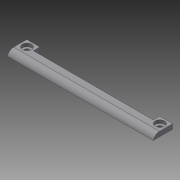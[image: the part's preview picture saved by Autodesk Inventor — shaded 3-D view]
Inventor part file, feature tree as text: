
AUTODESK INVENTOR PART (.ipt)
format: ipt  version: 2015 (Build 190159000, 159)  size: 122,368 bytes
history: native  units: mm
features: extrude x5, sketch x5, other x1, fillet x1
ambient origin geometry x8: Origin, YZ Plane, XZ Plane, XY Plane, X Axis, Y Axis, Z Axis, Center Point
bodies: Body1 (feature_tree), Body2 (feature_tree)
feature tree (12):
  other  "ソリッド1"
  extrude  "押し出し1"  Depth=90.0mm
  extrude  "押し出し2"  Depth=7.0mm
  extrude  "押し出し3"  Depth=3.0mm TaperAngle=0.0deg
  extrude  "押し出し4"  Depth=5.8mm
  fillet  "フィレット1"  Radius=5.8mm
  extrude  "押し出し5"  Depth=3.9mm
  sketch  "スケッチ1"
  sketch  "スケッチ2"
  sketch  "スケッチ3"
  sketch  "スケッチ4"
  sketch  "スケッチ6"
